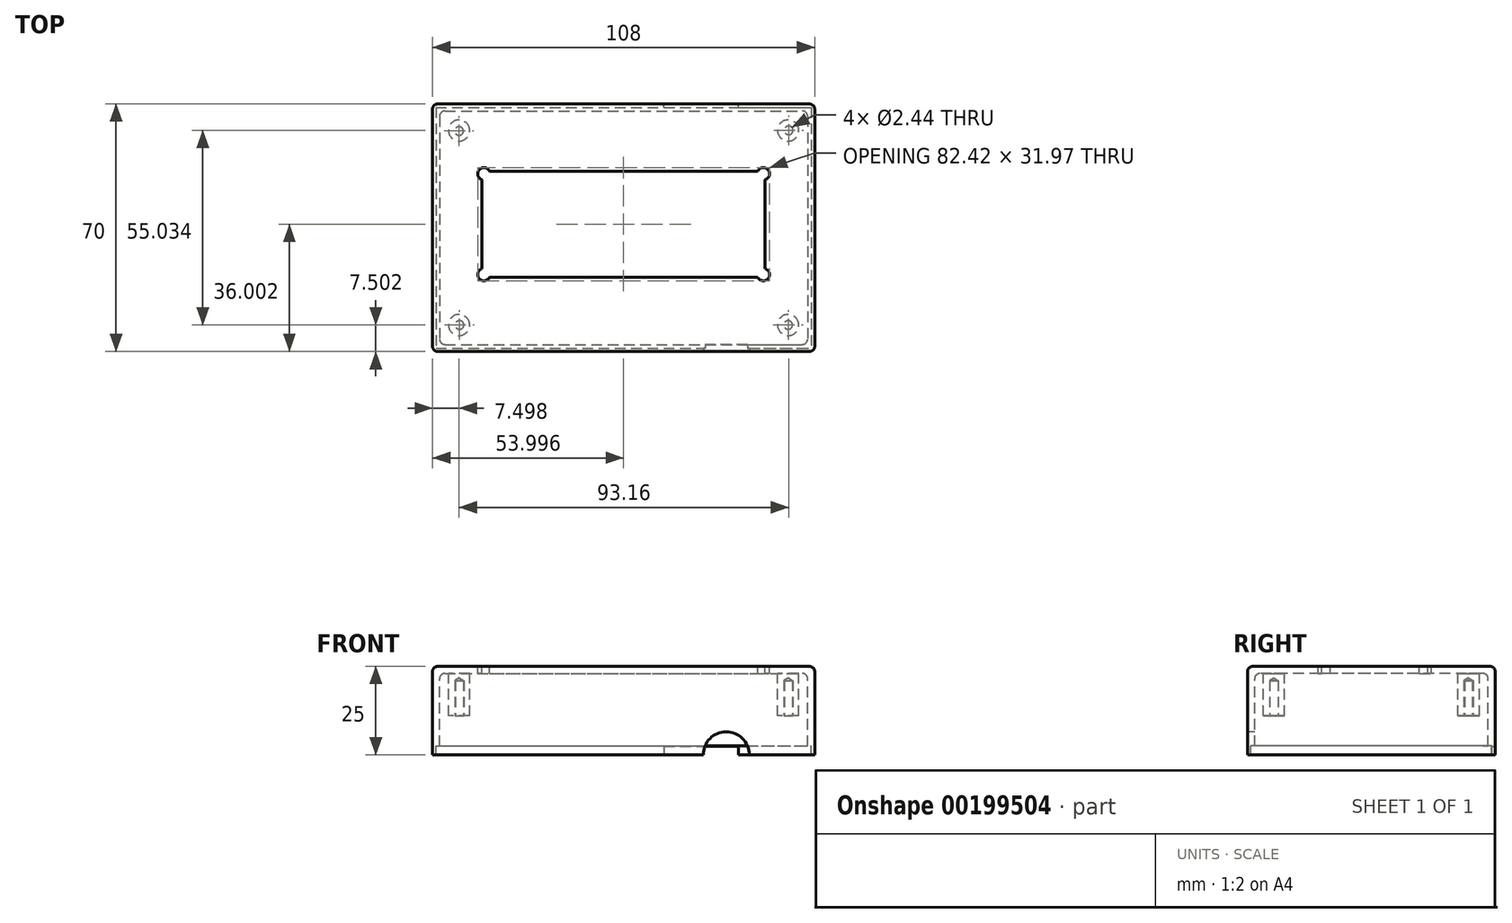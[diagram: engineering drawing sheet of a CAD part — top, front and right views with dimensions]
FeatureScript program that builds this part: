
annotation { "Feature Type Name" : "Feature", "Feature Type Description" : "" }
export const myFeature = defineFeature(function(context is Context, id is Id, definition is map)
    precondition{}
    {
        {
            var Q0;
            Q0=qCreatedBy(makeId("Top.planeOp"),FACE);
            var sketch = newSketch(context, id + "F0", { "sketchPlane" : qUnion([Q0])});
            skLineSegment(sketch, "E0.bottom", {"start": v(-57.35, 34.9) * mm, "end": v(50.65, 34.9) * mm});
            skLineSegment(sketch, "E0.top", {"start": v(-57.35, -35.1) * mm, "end": v(50.65, -35.1) * mm});
            skLineSegment(sketch, "E0.left", {"start": v(-57.35, 34.9) * mm, "end": v(-57.35, -35.1) * mm});
            skLineSegment(sketch, "E0.right", {"start": v(50.65, 34.9) * mm, "end": v(50.65, -35.1) * mm});
            skCircle(sketch, "E1", {"center": v(-42.85, 15.14) * mm, "radius": 1.75 * mm});
            skCircle(sketch, "E2", {"center": v(-42.85, -13.36) * mm, "radius": 1.75 * mm});
            skCircle(sketch, "E3", {"center": v(36.15, -13.36) * mm, "radius": 1.75 * mm});
            skCircle(sketch, "E4", {"center": v(36.15, 15.14) * mm, "radius": 1.75 * mm});
            skLineSegment(sketch, "E5.bottom", {"start": v(-55.35, 32.9) * mm, "end": v(48.65, 32.9) * mm});
            skLineSegment(sketch, "E5.top", {"start": v(-55.35, -33.1) * mm, "end": v(48.65, -33.1) * mm});
            skLineSegment(sketch, "E5.left", {"start": v(-55.35, 32.9) * mm, "end": v(-55.35, -33.1) * mm});
            skLineSegment(sketch, "E5.right", {"start": v(48.65, 32.9) * mm, "end": v(48.65, -33.1) * mm});
            skCircle(sketch, "E6", {"center": v(-49.85, 27.4) * mm, "radius": 3 * mm});
            skCircle(sketch, "E7", {"center": v(43.15, 27.4) * mm, "radius": 3 * mm});
            skCircle(sketch, "E8", {"center": v(-49.85, -27.6) * mm, "radius": 3 * mm});
            skCircle(sketch, "E9", {"center": v(43.15, -27.6) * mm, "radius": 3 * mm});
            skPoint(sketch, "E10.visualSharp", {"position": v(-55.35, -33.1) * mm});
            skPoint(sketch, "E11.visualSharp", {"position": v(-55.35, 32.9) * mm});
            skPoint(sketch, "E12.visualSharp", {"position": v(48.65, 32.9) * mm});
            skPoint(sketch, "E13.visualSharp", {"position": v(48.65, -33.1) * mm});
            skPoint(sketch, "E14.visualSharp", {"position": v(-57.35, 34.9) * mm});
            skPoint(sketch, "E15.visualSharp", {"position": v(50.65, 34.9) * mm});
            skPoint(sketch, "E16.visualSharp", {"position": v(50.65, -35.1) * mm});
            skLineSegment(sketch, "E17.bottom", {"start": v(-56.4, 33.94) * mm, "end": v(49.7, 33.94) * mm});
            skLineSegment(sketch, "E17.top", {"start": v(-56.4, -34.16) * mm, "end": v(49.7, -34.16) * mm});
            skLineSegment(sketch, "E17.left", {"start": v(-56.4, 33.94) * mm, "end": v(-56.4, -34.16) * mm});
            skLineSegment(sketch, "E17.right", {"start": v(49.7, 33.94) * mm, "end": v(49.7, -34.16) * mm});
            skLineSegment(sketch, "E18.bottom", {"start": v(-43.35, 15.9) * mm, "end": v(36.65, 15.9) * mm});
            skLineSegment(sketch, "E18.top", {"start": v(-43.35, -14.1) * mm, "end": v(36.65, -14.1) * mm});
            skLineSegment(sketch, "E18.left", {"start": v(-43.35, 15.9) * mm, "end": v(-43.35, -14.1) * mm});
            skLineSegment(sketch, "E18.right", {"start": v(36.65, 15.9) * mm, "end": v(36.65, -14.1) * mm});
            skSolve(sketch);
        }
        {
            var Q0;
            Q0=makeQuery(id+"F0.imprint","IMPRINT",FACE,{"disambiguationData":[TD([[makeQuery(id+"F0.imprint","IMPRINT",EDGE,{"derivedFrom":sQuery(id+"F0.wireOp",EDGE,"E5.bottom")}),1.0]])]});
            var Q1;
            Q1=makeQuery(id+"F0.imprint","IMPRINT",FACE,{"disambiguationData":[TD([[makeQuery(id+"F0.imprint","IMPRINT",EDGE,{"derivedFrom":sQuery(id+"F0.wireOp",EDGE,"E5.bottom")}),-1.0]])]});
            var Q2;
            Q2=makeQuery(id+"F0.imprint","IMPRINT",FACE,{"disambiguationData":[TD([[makeQuery(id+"F0.imprint","IMPRINT",EDGE,{"derivedFrom":sQuery(id+"F0.wireOp",EDGE,"E6")}),1.0]])]});
            var Q3;
            Q3=makeQuery(id+"F0.imprint","IMPRINT",FACE,{"disambiguationData":[TD([[makeQuery(id+"F0.imprint","IMPRINT",EDGE,{"derivedFrom":sQuery(id+"F0.wireOp",EDGE,"E7")}),1.0]])]});
            var Q4;
            Q4=makeQuery(id+"F0.imprint","IMPRINT",FACE,{"disambiguationData":[TD([[makeQuery(id+"F0.imprint","IMPRINT",EDGE,{"derivedFrom":sQuery(id+"F0.wireOp",EDGE,"E9")}),1.0]])]});
            var Q5;
            Q5=makeQuery(id+"F0.imprint","IMPRINT",FACE,{"disambiguationData":[TD([[makeQuery(id+"F0.imprint","IMPRINT",EDGE,{"derivedFrom":sQuery(id+"F0.wireOp",EDGE,"E8")}),1.0]])]});
            var Q6;
            Q6=makeQuery(id+"F0.imprint","IMPRINT",FACE,{"disambiguationData":[TD([[makeQuery(id+"F0.imprint","IMPRINT",EDGE,{"derivedFrom":sQuery(id+"F0.wireOp",EDGE,"E0.bottom")}),-1.0]])]});
            extrude(context, id + "F1", {"entities" : qUnion([Q0, Q1, Q2, Q3, Q4, Q5, Q6]), "oppositeDirection" : true, "depth" : 2 * mm});
        }
        {
            var Q0;
            Q0=makeQuery(id+"F0.imprint","IMPRINT",FACE,{"disambiguationData":[TD([[makeQuery(id+"F0.imprint","IMPRINT",EDGE,{"derivedFrom":sQuery(id+"F0.wireOp",EDGE,"E5.bottom")}),1.0]])]});
            extrude(context, id + "F2", {"entities" : qUnion([Q0]), "operationType" : NewBodyOperationType.ADD, "oppositeDirection" : true, "depth" : 22.49 * mm});
        }
        {
            var Q0;
            {var subQ0=sQuery(id+"F0.wireOp",EDGE,"E0.right");var subQ1=sQuery(id+"F0.wireOp",EDGE,"E0.left");var subQ2=sQuery(id+"F0.wireOp",EDGE,"E0.top");var subQ3=sQuery(id+"F0.wireOp",EDGE,"E0.bottom");Q0=makeQuery(id+"F2.boolean.opBoolean","SPLIT",FACE,{"disambiguationData":[TD([makeQuery(id+"F1.opExtrude","SWEPT_FACE",FACE,{"disambiguationData":[OSD([subQ3])]})])],"derivedFrom":makeQuery(id+"F1.opExtrude","CAP_FACE",FACE,{"disambiguationData":[OSD([subQ3,subQ2,subQ1,subQ0,sQuery(id+"F0.wireOp",EDGE,"GkgKN4X4-4t61-OEX7-k9zT-44ioRnZ2twka.bottom"),sQuery(id+"F0.wireOp",EDGE,"GkgKN4X4-4t61-OEX7-k9zT-44ioRnZ2twka.top"),sQuery(id+"F0.wireOp",EDGE,"GkgKN4X4-4t61-OEX7-k9zT-44ioRnZ2twka.left"),sQuery(id+"F0.wireOp",EDGE,"GkgKN4X4-4t61-OEX7-k9zT-44ioRnZ2twka.right"),sQuery(id+"F0.wireOp",EDGE,"E1"),sQuery(id+"F0.wireOp",EDGE,"E2"),sQuery(id+"F0.wireOp",EDGE,"E3"),sQuery(id+"F0.wireOp",EDGE,"E4")])],"isStart":false})});}
            extrude(context, id + "F3", {"entities" : qUnion([Q0]), "operationType" : NewBodyOperationType.ADD, "depth" : 23 * mm});
        }
        {
            var Q0;
            Q0=makeQuery(id+"F0.imprint","IMPRINT",FACE,{"disambiguationData":[TD([[makeQuery(id+"F0.imprint","IMPRINT",EDGE,{"derivedFrom":sQuery(id+"F0.wireOp",EDGE,"E6")}),1.0]])]});
            var Q1;
            Q1=makeQuery(id+"F0.imprint","IMPRINT",FACE,{"disambiguationData":[TD([[makeQuery(id+"F0.imprint","IMPRINT",EDGE,{"derivedFrom":sQuery(id+"F0.wireOp",EDGE,"E7")}),1.0]])]});
            var Q2;
            Q2=makeQuery(id+"F0.imprint","IMPRINT",FACE,{"disambiguationData":[TD([[makeQuery(id+"F0.imprint","IMPRINT",EDGE,{"derivedFrom":sQuery(id+"F0.wireOp",EDGE,"E8")}),1.0]])]});
            var Q3;
            Q3=makeQuery(id+"F0.imprint","IMPRINT",FACE,{"disambiguationData":[TD([[makeQuery(id+"F0.imprint","IMPRINT",EDGE,{"derivedFrom":sQuery(id+"F0.wireOp",EDGE,"E9")}),1.0]])]});
            extrude(context, id + "F4", {"entities" : qUnion([Q0, Q1, Q2, Q3]), "operationType" : NewBodyOperationType.ADD, "oppositeDirection" : true, "depth" : 14 * mm});
        }
        {
            var Q0;
            {var subQ0=sQuery(id+"F0.wireOp",EDGE,"E0.top");Q0=makeQuery(id+"F3.boolean.opBoolean","MERGE",FACE,{"derivedFrom":[makeQuery(id+"F1.opExtrude","SWEPT_FACE",FACE,{"disambiguationData":[OSD([subQ0])]}),makeQuery(id+"F3.opExtrude","SWEPT_FACE",FACE,{"disambiguationData":[OSD([subQ0])]})]});}
            var sketch = newSketch(context, id + "F5", { "sketchPlane" : qUnion([Q0])});
            skPoint(sketch, "E19", {"position": v(25.65, -25) * mm});
            skCircle(sketch, "E20", {"center": v(25.65, -25) * mm, "radius": 6.5 * mm});
            skSolve(sketch);
        }
        {
            var Q0;
            {var subQ0=sQuery(id+"F5.wireOp",EDGE,"E20");var subQ1=makeQuery(id+"F3.opExtrude","CAP_EDGE",EDGE,{"disambiguationData":[OSD([sQuery(id+"F0.wireOp",EDGE,"E0.top")])],"isStart":false});var subQ2=makeQuery(id+"F5.imprint","INTERSECT",VERTEX,{"disambiguationData":[OD(0.0)],"derivedFrom":[subQ1,subQ0]});Q0=makeQuery(id+"F5.imprint","IMPRINT",FACE,{"disambiguationData":[TD([[makeQuery(id+"F5.imprint","IMPRINT",EDGE,{"disambiguationData":[TD([[subQ2,1.0]])],"derivedFrom":subQ0}),1.0]])]});}
            extrude(context, id + "F6", {"entities" : qUnion([Q0]), "operationType" : NewBodyOperationType.REMOVE, "oppositeDirection" : true, "depth" : 2.5 * mm});
        }
        {
            var Q0;
            {var subQ0=sQuery(id+"F0.wireOp",EDGE,"E0.bottom");Q0=makeQuery(id+"F3.boolean.opBoolean","MERGE",FACE,{"derivedFrom":[makeQuery(id+"F1.opExtrude","SWEPT_FACE",FACE,{"disambiguationData":[OSD([subQ0])]}),makeQuery(id+"F3.opExtrude","SWEPT_FACE",FACE,{"disambiguationData":[OSD([subQ0])]})]});}
            var sketch = newSketch(context, id + "F7", { "sketchPlane" : qUnion([Q0])});
            skLineSegment(sketch, "E21.bottom", {"start": v(-29.05, -25) * mm, "end": v(-8.05, -25) * mm});
            skLineSegment(sketch, "E21.top", {"start": v(-29.05, -22.6) * mm, "end": v(-8.05, -22.6) * mm});
            skLineSegment(sketch, "E21.left", {"start": v(-29.05, -25) * mm, "end": v(-29.05, -22.6) * mm});
            skLineSegment(sketch, "E21.right", {"start": v(-8.05, -25) * mm, "end": v(-8.05, -22.6) * mm});
            skSolve(sketch);
        }
        {
            var Q0;
            Q0=makeQuery(id+"F7.imprint","IMPRINT",FACE,{"disambiguationData":[TD([[makeQuery(id+"F7.imprint","IMPRINT",EDGE,{"derivedFrom":sQuery(id+"F7.wireOp",EDGE,"E21.bottom")}),-1.0]])]});
            extrude(context, id + "F8", {"entities" : qUnion([Q0]), "operationType" : NewBodyOperationType.REMOVE, "oppositeDirection" : true, "depth" : 2.5 * mm});
        }
        {
            var Q0;
            Q0=makeQuery(id+"F4.opExtrude","CAP_FACE",FACE,{"disambiguationData":[OSD([sQuery(id+"F0.wireOp",EDGE,"E9")])],"isStart":false});
            var sketch = newSketch(context, id + "F9", { "sketchPlane" : qUnion([Q0])});
            skPoint(sketch, "E22", {"position": v(-49.85, -27.23) * mm});
            skPoint(sketch, "E23", {"position": v(43.3, -27.43) * mm});
            skPoint(sketch, "E24", {"position": v(43.15, 27.6) * mm});
            skPoint(sketch, "E25", {"position": v(-49.73, 27.6) * mm});
            skSolve(sketch);
        }
        {
            var Q0;
            Q0=sQuery(id+"F9.wireOp",VERTEX,"E22");
            var Q1;
            Q1=sQuery(id+"F9.wireOp",VERTEX,"E23");
            var Q2;
            Q2=sQuery(id+"F9.wireOp",VERTEX,"E24");
            var Q3;
            Q3=sQuery(id+"F9.wireOp",VERTEX,"E25");
            var Q4;
            Q4=makeQuery(id+"F1.opExtrude","SWEPT_BODY",BODY,{"disambiguationData":[OSD([sQuery(id+"F0.wireOp",EDGE,"E0.bottom"),sQuery(id+"F0.wireOp",EDGE,"E0.top"),sQuery(id+"F0.wireOp",EDGE,"E0.left"),sQuery(id+"F0.wireOp",EDGE,"E0.right"),sQuery(id+"F0.wireOp",EDGE,"GkgKN4X4-4t61-OEX7-k9zT-44ioRnZ2twka.bottom"),sQuery(id+"F0.wireOp",EDGE,"GkgKN4X4-4t61-OEX7-k9zT-44ioRnZ2twka.top"),sQuery(id+"F0.wireOp",EDGE,"GkgKN4X4-4t61-OEX7-k9zT-44ioRnZ2twka.left"),sQuery(id+"F0.wireOp",EDGE,"GkgKN4X4-4t61-OEX7-k9zT-44ioRnZ2twka.right"),sQuery(id+"F0.wireOp",EDGE,"E1"),sQuery(id+"F0.wireOp",EDGE,"E2"),sQuery(id+"F0.wireOp",EDGE,"E3"),sQuery(id+"F0.wireOp",EDGE,"E4")])]});
            hole(context, id + "F10", {"style" : HoleStyle.SIMPLE, "endStyle" : HoleEndStyle.BLIND, "standardTappedOrClearance" : lookupTablePath({ "standard" : "ANSI", "size" : "#41 (0.1)", "type" : "Drilled" }), "standardBlindInLast" : lookupTablePath({ "standard" : "ANSI", "size" : "#41", "type" : "Drilled" }), "holeDiameter" : 2.44 * mm, "holeDepth" : 10 * mm, "tappedDepth" : 12 * mm, "tapClearance" : 3, "startFromSketch" : true, "locations" : qUnion([Q0, Q1, Q2, Q3]), "scope" : qUnion([Q4])});
        }
        {
            var Q0;
            Q0=makeQuery(id+"F1.opExtrude","CAP_EDGE",EDGE,{"disambiguationData":[OSD([sQuery(id+"F0.wireOp",EDGE,"E0.left")])],"isStart":true});
            var Q1;
            Q1=makeQuery(id+"F1.opExtrude","CAP_EDGE",EDGE,{"disambiguationData":[OSD([sQuery(id+"F0.wireOp",EDGE,"E0.bottom")])],"isStart":true});
            var Q2;
            Q2=makeQuery(id+"F1.opExtrude","CAP_EDGE",EDGE,{"disambiguationData":[OSD([sQuery(id+"F0.wireOp",EDGE,"E0.right")])],"isStart":true});
            var Q3;
            {var subQ0=sQuery(id+"F0.wireOp",EDGE,"E0.right");var subQ1=sQuery(id+"F0.wireOp",EDGE,"E0.top");Q3=makeQuery(id+"F3.boolean.opBoolean","MERGE",EDGE,{"derivedFrom":[makeQuery(id+"F1.opExtrude","SWEPT_EDGE",EDGE,{"disambiguationData":[OSD([subQ1,subQ0])]}),makeQuery(id+"F3.opExtrude","SWEPT_EDGE",EDGE,{"disambiguationData":[OSD([subQ1,subQ0])]})]});}
            var Q4;
            Q4=makeQuery(id+"F1.opExtrude","CAP_EDGE",EDGE,{"disambiguationData":[OSD([sQuery(id+"F0.wireOp",EDGE,"E0.top")])],"isStart":true});
            var Q5;
            {var subQ0=sQuery(id+"F0.wireOp",EDGE,"E0.left");var subQ1=sQuery(id+"F0.wireOp",EDGE,"E0.top");Q5=makeQuery(id+"F3.boolean.opBoolean","MERGE",EDGE,{"derivedFrom":[makeQuery(id+"F1.opExtrude","SWEPT_EDGE",EDGE,{"disambiguationData":[OSD([subQ1,subQ0])]}),makeQuery(id+"F3.opExtrude","SWEPT_EDGE",EDGE,{"disambiguationData":[OSD([subQ1,subQ0])]})]});}
            var Q6;
            {var subQ0=sQuery(id+"F0.wireOp",EDGE,"E0.right");var subQ1=sQuery(id+"F0.wireOp",EDGE,"E0.bottom");Q6=makeQuery(id+"F3.boolean.opBoolean","MERGE",EDGE,{"derivedFrom":[makeQuery(id+"F1.opExtrude","SWEPT_EDGE",EDGE,{"disambiguationData":[OSD([subQ1,subQ0])]}),makeQuery(id+"F3.opExtrude","SWEPT_EDGE",EDGE,{"disambiguationData":[OSD([subQ1,subQ0])]})]});}
            var Q7;
            {var subQ0=sQuery(id+"F0.wireOp",EDGE,"E0.left");var subQ1=sQuery(id+"F0.wireOp",EDGE,"E0.bottom");Q7=makeQuery(id+"F3.boolean.opBoolean","MERGE",EDGE,{"derivedFrom":[makeQuery(id+"F1.opExtrude","SWEPT_EDGE",EDGE,{"disambiguationData":[OSD([subQ1,subQ0])]}),makeQuery(id+"F3.opExtrude","SWEPT_EDGE",EDGE,{"disambiguationData":[OSD([subQ1,subQ0])]})]});}
            fillet(context, id + "F11", {"entities" : qUnion([Q0, Q1, Q2, Q3, Q4, Q5, Q6, Q7]), "radius" : 1.5 * mm, "tangentPropagation" : true, "allowEdgeOverflow" : false});
        }
        {
            var Q0;
            Q0=makeQuery(id+"F2.opExtrude","SWEPT_EDGE",EDGE,{"disambiguationData":[OSD([sQuery(id+"F0.wireOp",EDGE,"E5.top"),sQuery(id+"F0.wireOp",EDGE,"E5.right")])]});
            var Q1;
            Q1=makeQuery(id+"F2.boolean.opBoolean","INTERSECT",EDGE,{"derivedFrom":[makeQuery(id+"F1.opExtrude","CAP_FACE",FACE,{"disambiguationData":[OSD([sQuery(id+"F0.wireOp",EDGE,"E0.bottom"),sQuery(id+"F0.wireOp",EDGE,"E0.top"),sQuery(id+"F0.wireOp",EDGE,"E0.left"),sQuery(id+"F0.wireOp",EDGE,"E0.right"),sQuery(id+"F0.wireOp",EDGE,"GkgKN4X4-4t61-OEX7-k9zT-44ioRnZ2twka.bottom"),sQuery(id+"F0.wireOp",EDGE,"GkgKN4X4-4t61-OEX7-k9zT-44ioRnZ2twka.top"),sQuery(id+"F0.wireOp",EDGE,"GkgKN4X4-4t61-OEX7-k9zT-44ioRnZ2twka.left"),sQuery(id+"F0.wireOp",EDGE,"GkgKN4X4-4t61-OEX7-k9zT-44ioRnZ2twka.right"),sQuery(id+"F0.wireOp",EDGE,"E1"),sQuery(id+"F0.wireOp",EDGE,"E2"),sQuery(id+"F0.wireOp",EDGE,"E3"),sQuery(id+"F0.wireOp",EDGE,"E4")])],"isStart":false}),makeQuery(id+"F2.opExtrude","SWEPT_FACE",FACE,{"disambiguationData":[OSD([sQuery(id+"F0.wireOp",EDGE,"E5.right")])]})]});
            var Q2;
            Q2=makeQuery(id+"F2.boolean.opBoolean","INTERSECT",EDGE,{"derivedFrom":[makeQuery(id+"F1.opExtrude","CAP_FACE",FACE,{"disambiguationData":[OSD([sQuery(id+"F0.wireOp",EDGE,"E0.bottom"),sQuery(id+"F0.wireOp",EDGE,"E0.top"),sQuery(id+"F0.wireOp",EDGE,"E0.left"),sQuery(id+"F0.wireOp",EDGE,"E0.right"),sQuery(id+"F0.wireOp",EDGE,"GkgKN4X4-4t61-OEX7-k9zT-44ioRnZ2twka.bottom"),sQuery(id+"F0.wireOp",EDGE,"GkgKN4X4-4t61-OEX7-k9zT-44ioRnZ2twka.top"),sQuery(id+"F0.wireOp",EDGE,"GkgKN4X4-4t61-OEX7-k9zT-44ioRnZ2twka.left"),sQuery(id+"F0.wireOp",EDGE,"GkgKN4X4-4t61-OEX7-k9zT-44ioRnZ2twka.right"),sQuery(id+"F0.wireOp",EDGE,"E1"),sQuery(id+"F0.wireOp",EDGE,"E2"),sQuery(id+"F0.wireOp",EDGE,"E3"),sQuery(id+"F0.wireOp",EDGE,"E4")])],"isStart":false}),makeQuery(id+"F2.opExtrude","SWEPT_FACE",FACE,{"disambiguationData":[OSD([sQuery(id+"F0.wireOp",EDGE,"E5.top")])]})]});
            var Q3;
            Q3=makeQuery(id+"F2.opExtrude","SWEPT_EDGE",EDGE,{"disambiguationData":[OSD([sQuery(id+"F0.wireOp",EDGE,"E5.top"),sQuery(id+"F0.wireOp",EDGE,"E5.left")])]});
            var Q4;
            Q4=makeQuery(id+"F2.boolean.opBoolean","INTERSECT",EDGE,{"derivedFrom":[makeQuery(id+"F1.opExtrude","CAP_FACE",FACE,{"disambiguationData":[OSD([sQuery(id+"F0.wireOp",EDGE,"E0.bottom"),sQuery(id+"F0.wireOp",EDGE,"E0.top"),sQuery(id+"F0.wireOp",EDGE,"E0.left"),sQuery(id+"F0.wireOp",EDGE,"E0.right"),sQuery(id+"F0.wireOp",EDGE,"GkgKN4X4-4t61-OEX7-k9zT-44ioRnZ2twka.bottom"),sQuery(id+"F0.wireOp",EDGE,"GkgKN4X4-4t61-OEX7-k9zT-44ioRnZ2twka.top"),sQuery(id+"F0.wireOp",EDGE,"GkgKN4X4-4t61-OEX7-k9zT-44ioRnZ2twka.left"),sQuery(id+"F0.wireOp",EDGE,"GkgKN4X4-4t61-OEX7-k9zT-44ioRnZ2twka.right"),sQuery(id+"F0.wireOp",EDGE,"E1"),sQuery(id+"F0.wireOp",EDGE,"E2"),sQuery(id+"F0.wireOp",EDGE,"E3"),sQuery(id+"F0.wireOp",EDGE,"E4")])],"isStart":false}),makeQuery(id+"F2.opExtrude","SWEPT_FACE",FACE,{"disambiguationData":[OSD([sQuery(id+"F0.wireOp",EDGE,"E5.left")])]})]});
            var Q5;
            Q5=makeQuery(id+"F2.opExtrude","SWEPT_EDGE",EDGE,{"disambiguationData":[OSD([sQuery(id+"F0.wireOp",EDGE,"E5.bottom"),sQuery(id+"F0.wireOp",EDGE,"E5.left")])]});
            var Q6;
            Q6=makeQuery(id+"F2.boolean.opBoolean","INTERSECT",EDGE,{"derivedFrom":[makeQuery(id+"F1.opExtrude","CAP_FACE",FACE,{"disambiguationData":[OSD([sQuery(id+"F0.wireOp",EDGE,"E0.bottom"),sQuery(id+"F0.wireOp",EDGE,"E0.top"),sQuery(id+"F0.wireOp",EDGE,"E0.left"),sQuery(id+"F0.wireOp",EDGE,"E0.right"),sQuery(id+"F0.wireOp",EDGE,"GkgKN4X4-4t61-OEX7-k9zT-44ioRnZ2twka.bottom"),sQuery(id+"F0.wireOp",EDGE,"GkgKN4X4-4t61-OEX7-k9zT-44ioRnZ2twka.top"),sQuery(id+"F0.wireOp",EDGE,"GkgKN4X4-4t61-OEX7-k9zT-44ioRnZ2twka.left"),sQuery(id+"F0.wireOp",EDGE,"GkgKN4X4-4t61-OEX7-k9zT-44ioRnZ2twka.right"),sQuery(id+"F0.wireOp",EDGE,"E1"),sQuery(id+"F0.wireOp",EDGE,"E2"),sQuery(id+"F0.wireOp",EDGE,"E3"),sQuery(id+"F0.wireOp",EDGE,"E4")])],"isStart":false}),makeQuery(id+"F2.opExtrude","SWEPT_FACE",FACE,{"disambiguationData":[OSD([sQuery(id+"F0.wireOp",EDGE,"E5.bottom")])]})]});
            var Q7;
            Q7=makeQuery(id+"F2.opExtrude","SWEPT_EDGE",EDGE,{"disambiguationData":[OSD([sQuery(id+"F0.wireOp",EDGE,"E5.bottom"),sQuery(id+"F0.wireOp",EDGE,"E5.right")])]});
            fillet(context, id + "F12", {"entities" : qUnion([Q0, Q1, Q2, Q3, Q4, Q5, Q6, Q7]), "radius" : 1.5 * mm, "tangentPropagation" : true, "allowEdgeOverflow" : false});
        }
    });
